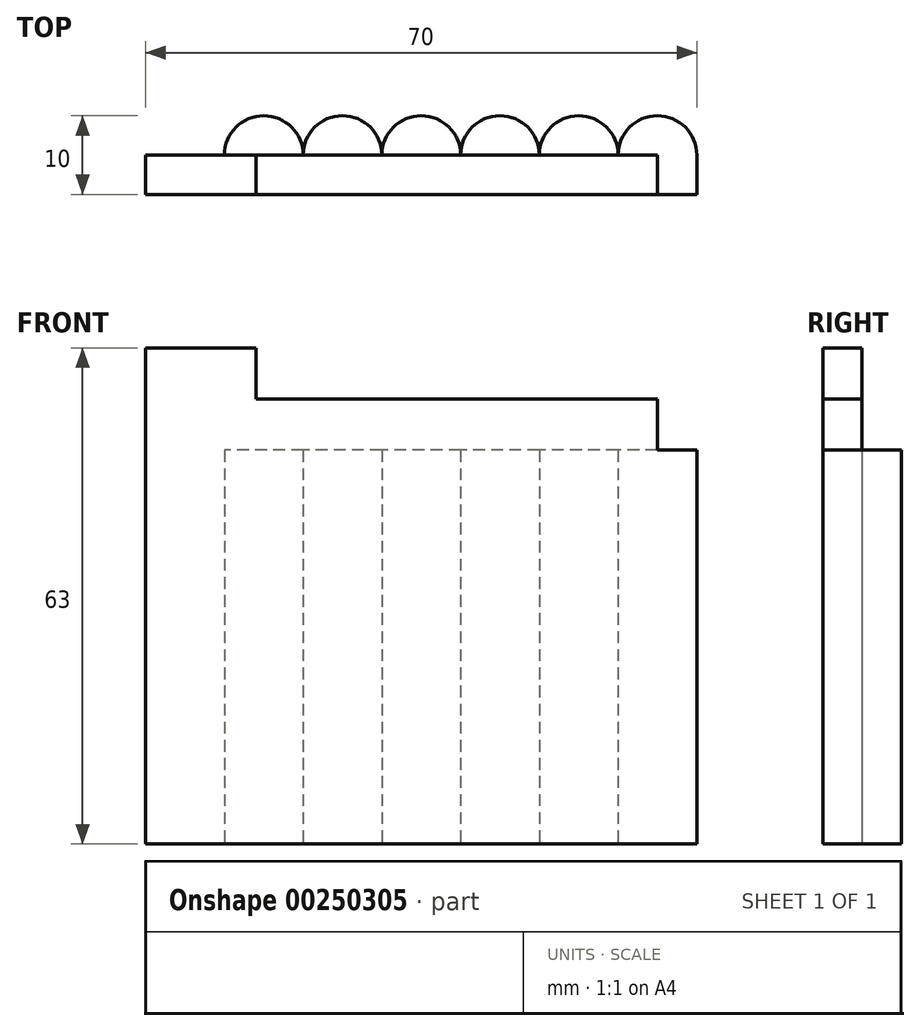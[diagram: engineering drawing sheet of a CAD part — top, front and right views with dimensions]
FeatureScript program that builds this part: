
annotation { "Feature Type Name" : "Feature", "Feature Type Description" : "" }
export const myFeature = defineFeature(function(context is Context, id is Id, definition is map)
    precondition{}
    {
        {
            var Q0;
            Q0=qCreatedBy(makeId("Top.planeOp"),FACE);
            var sketch = newSketch(context, id + "F0", { "sketchPlane" : qUnion([Q0])});
            skLineSegment(sketch, "E0", {"start": v(-32.03, 0) * mm, "end": v(37.97, 0) * mm});
            skLineSegment(sketch, "E1.0", {"start": v(-32.03, 5) * mm, "end": v(-22.03, 5) * mm});
            skArc(sketch, "E2", {"start": v(-12.03, 5) * mm, "mid": v(-17.03, 10) * mm, "end": v(-22.03, 5) * mm});
            skArc(sketch, "E3.1.0.0", {"start": v(-2.03, 5) * mm, "mid": v(-7.03, 10) * mm, "end": v(-12.03, 5) * mm});
            skArc(sketch, "E3.2.0.0", {"start": v(7.97, 5) * mm, "mid": v(2.97, 10) * mm, "end": v(-2.03, 5) * mm});
            skArc(sketch, "E3.3.0.0", {"start": v(17.97, 5) * mm, "mid": v(12.97, 10) * mm, "end": v(7.97, 5) * mm});
            skArc(sketch, "E3.4.0.0", {"start": v(27.97, 5) * mm, "mid": v(22.97, 10) * mm, "end": v(17.97, 5) * mm});
            skArc(sketch, "E3.5.0.0", {"start": v(37.97, 5) * mm, "mid": v(32.97, 10) * mm, "end": v(27.97, 5) * mm});
            skLineSegment(sketch, "E4.0", {"start": v(-32.03, 5) * mm, "end": v(-32.03, 0) * mm});
            skLineSegment(sketch, "E5", {"start": v(37.97, 5) * mm, "end": v(37.97, 0) * mm});
            skPoint(sketch, "E6.orphan", {"position": v(-42.78, 0) * mm});
            skSolve(sketch);
        }
        {
            var Q0;
            Q0=makeQuery(id+"F0.imprint","IMPRINT",FACE,{"disambiguationData":[TD([[makeQuery(id+"F0.imprint","IMPRINT",EDGE,{"derivedFrom":sQuery(id+"F0.wireOp",EDGE,"E0")}),1.0]])]});
            extrude(context, id + "F1", {"entities" : qUnion([Q0]), "depth" : 50 * mm});
        }
        {
            var Q0;
            Q0=makeQuery(id+"F1.opExtrude","CAP_FACE",FACE,{"disambiguationData":[OSD([sQuery(id+"F0.wireOp",EDGE,"E0"),sQuery(id+"F0.wireOp",EDGE,"E1.0"),sQuery(id+"F0.wireOp",EDGE,"E2"),sQuery(id+"F0.wireOp",EDGE,"E3.1.0.0"),sQuery(id+"F0.wireOp",EDGE,"E3.2.0.0"),sQuery(id+"F0.wireOp",EDGE,"E3.3.0.0"),sQuery(id+"F0.wireOp",EDGE,"E3.4.0.0"),sQuery(id+"F0.wireOp",EDGE,"E3.5.0.0"),sQuery(id+"F0.wireOp",EDGE,"E4.0"),sQuery(id+"F0.wireOp",EDGE,"E5")])],"isStart":false});
            var sketch = newSketch(context, id + "F2", { "sketchPlane" : qUnion([Q0])});
            skLineSegment(sketch, "E7.bottom", {"start": v(37.97, 0) * mm, "end": v(-32.03, 0) * mm});
            skLineSegment(sketch, "E7.top", {"start": v(37.97, 5) * mm, "end": v(-32.03, 5) * mm});
            skLineSegment(sketch, "E7.left", {"start": v(37.97, 0) * mm, "end": v(37.97, 5) * mm});
            skLineSegment(sketch, "E7.right", {"start": v(-32.03, 0) * mm, "end": v(-32.03, 5) * mm});
            skSolve(sketch);
        }
        {
            var Q0;
            Q0 = qSketchRegion(id + "F2", true);
            extrude(context, id + "F3", {"entities" : qUnion([Q0]), "operationType" : NewBodyOperationType.ADD, "depth" : 6.5 * mm});
        }
        {
            var Q0;
            Q0=makeQuery(id+"F3.opExtrude","CAP_FACE",FACE,{"disambiguationData":[OSD([sQuery(id+"F2.wireOp",EDGE,"E7.bottom"),sQuery(id+"F2.wireOp",EDGE,"E7.top"),sQuery(id+"F2.wireOp",EDGE,"E7.left"),sQuery(id+"F2.wireOp",EDGE,"E7.right")])],"isStart":false});
            var sketch = newSketch(context, id + "F4", { "sketchPlane" : qUnion([Q0])});
            skLineSegment(sketch, "E8", {"start": v(-32.03, 0) * mm, "end": v(-32.03, 15.26) * mm});
            skLineSegment(sketch, "E9.0", {"start": v(-18.03, 0) * mm, "end": v(-18.03, 15.26) * mm});
            skLineSegment(sketch, "E10.bottom", {"start": v(-32.03, 0) * mm, "end": v(-18.03, 0) * mm});
            skLineSegment(sketch, "E10.top", {"start": v(-32.03, 5) * mm, "end": v(-18.03, 5) * mm});
            skLineSegment(sketch, "E10.left", {"start": v(-32.03, 0) * mm, "end": v(-32.03, 5) * mm});
            skLineSegment(sketch, "E10.right", {"start": v(-18.03, 0) * mm, "end": v(-18.03, 5) * mm});
            skSolve(sketch);
        }
        {
            var Q0;
            Q0=makeQuery(id+"F3.boolean.opBoolean","MERGE",FACE,{"derivedFrom":[makeQuery(id+"F1.opExtrude","SWEPT_FACE",FACE,{"disambiguationData":[OSD([sQuery(id+"F0.wireOp",EDGE,"E5")])]}),makeQuery(id+"F3.opExtrude","SWEPT_FACE",FACE,{"disambiguationData":[OSD([sQuery(id+"F2.wireOp",EDGE,"E7.left")])]})]});
            var sketch = newSketch(context, id + "F5", { "sketchPlane" : qUnion([Q0])});
            skLineSegment(sketch, "E11.bottom", {"start": v(5, 50) * mm, "end": v(0, 50) * mm});
            skLineSegment(sketch, "E11.top", {"start": v(5, 56.5) * mm, "end": v(0, 56.5) * mm});
            skLineSegment(sketch, "E11.left", {"start": v(5, 50) * mm, "end": v(5, 56.5) * mm});
            skLineSegment(sketch, "E11.right", {"start": v(0, 50) * mm, "end": v(0, 56.5) * mm});
            skSolve(sketch);
        }
        {
            var Q0;
            Q0 = qSketchRegion(id + "F5", true);
            extrude(context, id + "F6", {"entities" : qUnion([Q0]), "operationType" : NewBodyOperationType.REMOVE, "oppositeDirection" : true, "depth" : 5 * mm});
        }
        {
            var Q0;
            Q0=makeQuery(id+"F4.imprint","IMPRINT",FACE,{"disambiguationData":[TD([[makeQuery(id+"F4.imprint","IMPRINT",EDGE,{"derivedFrom":sQuery(id+"F4.wireOp",EDGE,"E10.bottom")}),1.0]])]});
            extrude(context, id + "F7", {"entities" : qUnion([Q0]), "operationType" : NewBodyOperationType.ADD, "depth" : 6.5 * mm});
        }
    });
